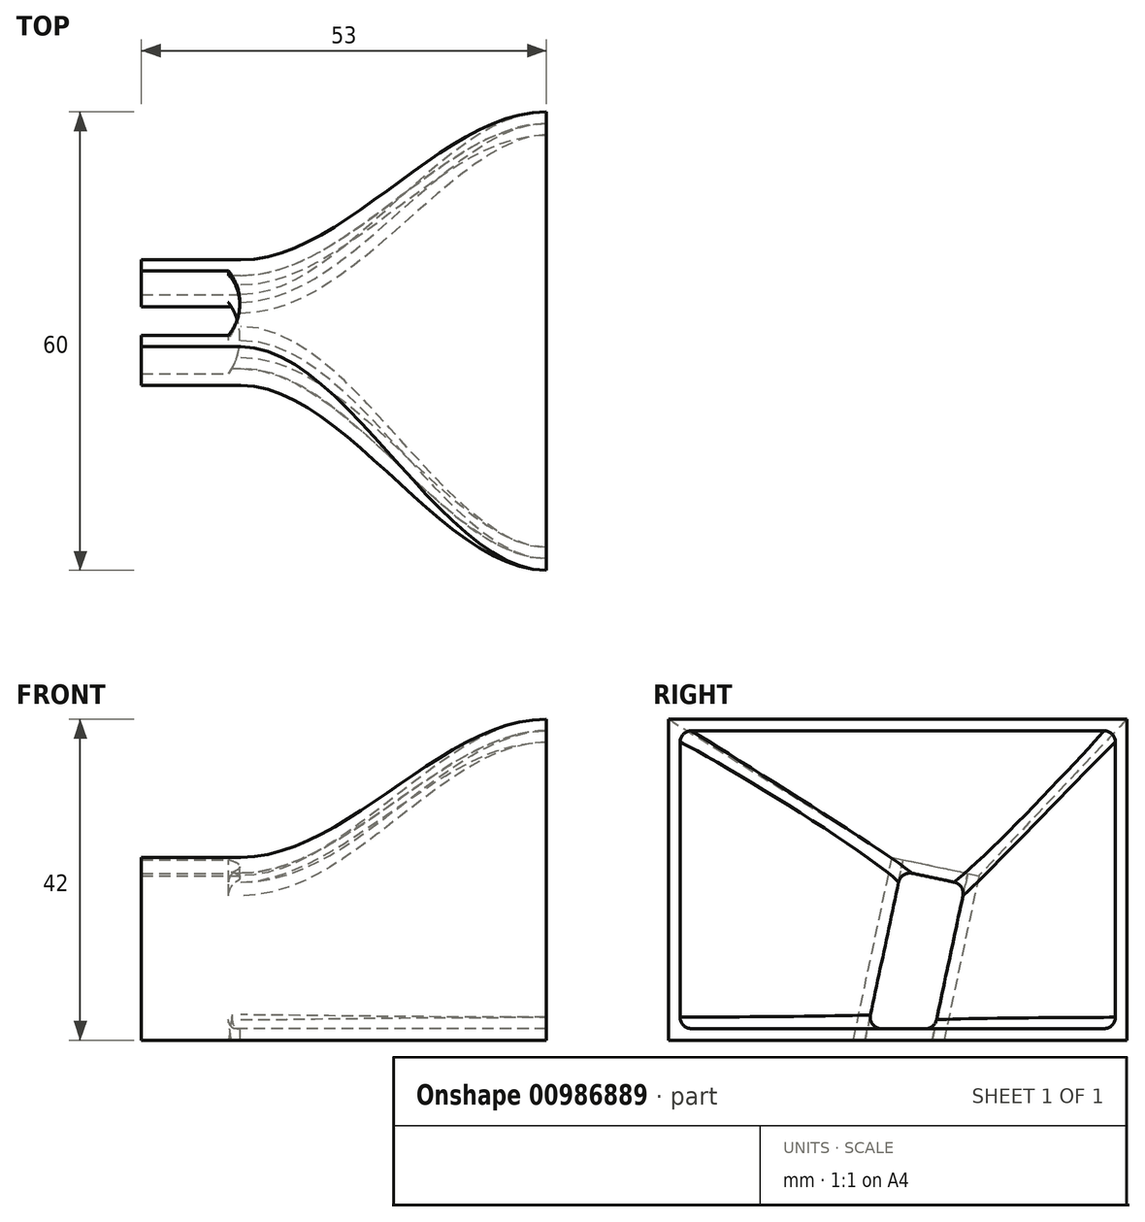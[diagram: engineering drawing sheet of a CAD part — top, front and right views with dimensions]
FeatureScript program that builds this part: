
annotation { "Feature Type Name" : "Feature", "Feature Type Description" : "" }
export const myFeature = defineFeature(function(context is Context, id is Id, definition is map)
    precondition{}
    {
        {
            var Q0;
            Q0=qCreatedBy(makeId("Top.planeOp"),FACE);
            var sketch = newSketch(context, id + "F0", { "sketchPlane" : qUnion([Q0])});
            skLineSegment(sketch, "E0", {"start": v(0, 6.05) * mm, "end": v(0, -6.05) * mm});
            skLineSegment(sketch, "E1", {"start": v(40, 30) * mm, "end": v(40, -30) * mm});
            skLineSegment(sketch, "E2", {"start": v(40, -30) * mm, "end": v(16.05, 0) * mm, "construction": true});
            skLineSegment(sketch, "E3", {"start": v(0, -6.05) * mm, "end": v(34.07, -6.05) * mm, "construction": true});
            skFitSpline(sketch, "E4", {"points": [v(0, -6.05) * mm, v(40, -30) * mm], "startDerivative": vector(33.29, 0) * mm, "endDerivative": vector(29.85, -37.4) * mm});
            skFitSpline(sketch, "E5.MirrorCS", {"points": [v(0, 6.05) * mm, v(40, 30) * mm], "startDerivative": vector(33.29, 0) * mm, "endDerivative": vector(29.85, 37.4) * mm});
            skSolve(sketch);
        }
        {
            var Q0;
            Q0=qCreatedBy(makeId("Right.planeOp"),FACE);
            var Q1;
            Q1=sQuery(id+"F0.wireOp",VERTEX,"E1.end");
            cPlane(context, id + "F1", {"entities" : qUnion([Q0, Q1]), "cplaneType" : CPlaneType.PLANE_POINT, "offset" : 25 * mm, "width" : 150 * mm, "height" : 150 * mm});
        }
        {
            var Q0;
            Q0=qCreatedBy(id+"F1.planeOp",FACE);
            var sketch = newSketch(context, id + "F2", { "sketchPlane" : qUnion([Q0])});
            skLineSegment(sketch, "E6.0", {"start": v(30, 0) * mm, "end": v(-30, 0) * mm});
            skLineSegment(sketch, "E7", {"start": v(-30, 0) * mm, "end": v(-30, 42) * mm});
            skLineSegment(sketch, "E8", {"start": v(-30, 42) * mm, "end": v(30, 42) * mm});
            skLineSegment(sketch, "E9", {"start": v(30, 42) * mm, "end": v(30, 0) * mm});
            skSolve(sketch);
        }
        {
            var Q0;
            Q0=qCreatedBy(makeId("Right.planeOp"),FACE);
            var sketch = newSketch(context, id + "F3", { "sketchPlane" : qUnion([Q0])});
            skPoint(sketch, "E10.0", {"position": v(6.05, 0) * mm});
            skLineSegment(sketch, "E11", {"start": v(-5.8, 0) * mm, "end": v(-0.72, 23.93) * mm});
            skLineSegment(sketch, "E12", {"start": v(-0.72, 23.93) * mm, "end": v(10.62, 21.52) * mm});
            skLineSegment(sketch, "E13", {"start": v(10.62, 21.52) * mm, "end": v(6.05, 0) * mm});
            skLineSegment(sketch, "E14", {"start": v(16.92, 0) * mm, "end": v(-15.5, 0) * mm, "construction": true});
            skLineSegment(sketch, "E15", {"start": v(6.05, 0) * mm, "end": v(-5.8, 0) * mm});
            skSolve(sketch);
        }
        {
            var Q0;
            Q0=sQuery(id+"F0.wireOp",EDGE,"E5.MirrorCS");
            var Q1;
            Q1=makeQuery(id+"F2.imprint","IMPRINT",FACE,{"disambiguationData":[TD([[makeQuery(id+"F2.imprint","IMPRINT",EDGE,{"derivedFrom":sQuery(id+"F2.wireOp",EDGE,"E6.0")}),-1.0]])]});
            var Q2;
            Q2=makeQuery(id+"F3.imprint","IMPRINT",FACE,{"disambiguationData":[TD([[makeQuery(id+"F3.imprint","IMPRINT",EDGE,{"derivedFrom":sQuery(id+"F3.wireOp",EDGE,"E11")}),-1.0]])]});
            var Q3;
            Q3=sQuery(id+"F0.wireOp",EDGE,"E5.MirrorCS");
            loft(context, id + "F4", {"spine" : qUnion([Q0]), "startCondition" : LoftEndDerivativeType.NORMAL_TO_PROFILE, "startMagnitude" : 1, "endCondition" : LoftEndDerivativeType.NORMAL_TO_PROFILE, "endMagnitude" : 1, "sheetProfilesArray" : [{ "sheetProfileEntities" : qUnion([Q1]) }, { "sheetProfileEntities" : qUnion([Q2]) }], "guidesArray" : [{ "guideEntities" : qUnion([Q3]), "guideDerivativeType" : LoftGuideDerivativeType.DEFAULT, "guideDerivativeMagnitude" : 1 }]});
        }
        {
            var Q0;
            Q0=makeQuery(id+"F4.opLoft","CAP_FACE",FACE,{"disambiguationData":[OSD([makeQuery(id+"F2.imprint","IMPRINT",FACE,{"disambiguationData":[TD([[makeQuery(id+"F2.imprint","IMPRINT",EDGE,{"derivedFrom":sQuery(id+"F2.wireOp",EDGE,"E6.0")}),-1.0]])]})])],"isStart":true});
            var Q1;
            Q1=makeQuery(id+"F4.opLoft","CAP_FACE",FACE,{"disambiguationData":[OSD([makeQuery(id+"F3.imprint","IMPRINT",FACE,{"disambiguationData":[TD([[makeQuery(id+"F3.imprint","IMPRINT",EDGE,{"derivedFrom":sQuery(id+"F3.wireOp",EDGE,"E11")}),-1.0]])]})])],"isStart":true});
            shell(context, id + "F5", {"entities" : qUnion([Q0, Q1]), "thickness" : 1.5 * mm});
        }
        {
            var Q0;
            Q0=qCreatedBy(makeId("Right.planeOp"),FACE);
            var sketch = newSketch(context, id + "F6", { "sketchPlane" : qUnion([Q0])});
            skLineSegment(sketch, "E16.0", {"start": v(10.62, 21.52) * mm, "end": v(6.05, 0) * mm});
            skLineSegment(sketch, "E16.3", {"start": v(-0.72, 23.93) * mm, "end": v(0.74, 23.62) * mm});
            skLineSegment(sketch, "E16.4", {"start": v(-5.8, 0) * mm, "end": v(-0.72, 23.93) * mm});
            skLineSegment(sketch, "E16.7", {"start": v(6.05, 0) * mm, "end": v(4.52, 0) * mm});
            skLineSegment(sketch, "E17.0", {"start": v(9.16, 21.83) * mm, "end": v(4.52, 0) * mm});
            skLineSegment(sketch, "E18.0", {"start": v(-4.28, 0) * mm, "end": v(0.74, 23.62) * mm});
            skLineSegment(sketch, "E19.trimOffspring", {"start": v(-4.28, 0) * mm, "end": v(-5.8, 0) * mm});
            skLineSegment(sketch, "E20.trimOffspring", {"start": v(9.16, 21.83) * mm, "end": v(10.62, 21.52) * mm});
            skSolve(sketch);
        }
        {
            var Q0;
            Q0 = qSketchRegion(id + "F6", true);
            extrude(context, id + "F7", {"entities" : qUnion([Q0]), "operationType" : NewBodyOperationType.ADD, "oppositeDirection" : true, "depth" : 13 * mm, "offsetDistance" : 25 * mm});
        }
        {
            var Q0;
            Q0=qCreatedBy(makeId("Top.planeOp"),FACE);
            var sketch = newSketch(context, id + "F8", { "sketchPlane" : qUnion([Q0])});
            skLineSegment(sketch, "E21.0", {"start": v(0, 6.05) * mm, "end": v(0, -6.05) * mm, "construction": true});
            skLineSegment(sketch, "E21.1", {"start": v(-13, 4.52) * mm, "end": v(0, 4.52) * mm, "construction": true});
            skLineSegment(sketch, "E21.2", {"start": v(-13, -4.28) * mm, "end": v(0, -4.28) * mm, "construction": true});
            skLineSegment(sketch, "E22", {"start": v(-1.5, 4.52) * mm, "end": v(0, 4.52) * mm});
            skLineSegment(sketch, "E23", {"start": v(0, 4.52) * mm, "end": v(0, -4.28) * mm});
            skLineSegment(sketch, "E24", {"start": v(-1.5, -4.28) * mm, "end": v(0, -4.28) * mm});
            skLineSegment(sketch, "E25.0", {"start": v(-13, 5.02) * mm, "end": v(0.01, 5.02) * mm, "construction": true});
            skArc(sketch, "E26", {"start": v(-1.6, -4.28) * mm, "mid": v(-0.1, 0.37) * mm, "end": v(-1.59, 5.02) * mm});
            skLineSegment(sketch, "E27", {"start": v(-1.59, 5.02) * mm, "end": v(0.01, 5.02) * mm});
            skLineSegment(sketch, "E28", {"start": v(0.01, 5.02) * mm, "end": v(0, -4.28) * mm});
            skLineSegment(sketch, "E29", {"start": v(0, -4.28) * mm, "end": v(-1.6, -4.28) * mm});
            skSolve(sketch);
        }
        {
            var Q0;
            {var subQ4=sQuery(id+"F8.wireOp",EDGE,"E23");Q0=makeQuery(id+"F8.imprint","IMPRINT",FACE,{"disambiguationData":[TD([[makeQuery(id+"F8.imprint","IMPRINT",EDGE,{"derivedFrom":subQ4}),1.0]])]});}
            var Q1;
            {var subQ0=sQuery(id+"F8.wireOp",EDGE,"E23");Q1=makeQuery(id+"F8.imprint","IMPRINT",FACE,{"disambiguationData":[TD([[makeQuery(id+"F8.imprint","IMPRINT",EDGE,{"derivedFrom":subQ0}),-1.0]])]});}
            extrude(context, id + "F9", {"entities" : qUnion([Q0, Q1]), "operationType" : NewBodyOperationType.ADD, "depth" : 1.5 * mm, "offsetDistance" : 25 * mm});
        }
        {
            var Q0;
            Q0=makeQuery(id+"F7.opExtrude","SWEPT_FACE",FACE,{"disambiguationData":[OSD([sQuery(id+"F6.wireOp",EDGE,"E16.3")])]});
            var sketch = newSketch(context, id + "F10", { "sketchPlane" : qUnion([Q0])});
            skLineSegment(sketch, "E30.0", {"start": v(-13, -4.18) * mm, "end": v(0, -4.18) * mm, "construction": true});
            skLineSegment(sketch, "E30.1", {"start": v(-13, 4.42) * mm, "end": v(0, 4.42) * mm, "construction": true});
            skLineSegment(sketch, "E30.2", {"start": v(0.01, 4.9) * mm, "end": v(0, -4.18) * mm, "construction": true});
            skArc(sketch, "E31", {"start": v(-1.6, -4.18) * mm, "mid": v(-0.12, 0.12) * mm, "end": v(-1.6, 4.42) * mm});
            skLineSegment(sketch, "E32", {"start": v(-1.6, -4.18) * mm, "end": v(0, -4.18) * mm});
            skLineSegment(sketch, "E33", {"start": v(0, -4.18) * mm, "end": v(0, 4.42) * mm});
            skLineSegment(sketch, "E34", {"start": v(0, 4.42) * mm, "end": v(-1.6, 4.42) * mm});
            skSolve(sketch);
        }
        {
            var Q0;
            Q0=makeQuery(id+"F10.imprint","IMPRINT",FACE,{"disambiguationData":[TD([[makeQuery(id+"F10.imprint","IMPRINT",EDGE,{"derivedFrom":sQuery(id+"F10.wireOp",EDGE,"E31")}),-1.0]])]});
            extrude(context, id + "F11", {"entities" : qUnion([Q0]), "operationType" : NewBodyOperationType.ADD, "oppositeDirection" : true, "depth" : 1.5 * mm, "offsetDistance" : 25 * mm});
        }
        {
            var Q0;
            Q0=makeQuery(id+"F5.opShell","OFFSET_EDGE",EDGE,{"disambiguationData":[OSD([sQuery(id+"F2.wireOp",EDGE,"E8"),sQuery(id+"F2.wireOp",EDGE,"E9"),sQuery(id+"F3.wireOp",EDGE,"E12"),sQuery(id+"F3.wireOp",EDGE,"E13")])]});
            var Q1;
            Q1=makeQuery(id+"F11.opExtrude","CAP_EDGE",EDGE,{"disambiguationData":[OSD([sQuery(id+"F10.wireOp",EDGE,"E34")])],"isStart":false});
            var Q2;
            Q2=makeQuery(id+"F5.opShell","OFFSET_EDGE",EDGE,{"disambiguationData":[OSD([sQuery(id+"F2.wireOp",EDGE,"E7"),sQuery(id+"F2.wireOp",EDGE,"E8"),sQuery(id+"F3.wireOp",EDGE,"E11"),sQuery(id+"F3.wireOp",EDGE,"E12")])]});
            var Q3;
            Q3=makeQuery(id+"F5.opShell","OFFSET_EDGE",EDGE,{"disambiguationData":[OSD([sQuery(id+"F2.wireOp",EDGE,"E6.0"),sQuery(id+"F2.wireOp",EDGE,"E7"),sQuery(id+"F3.wireOp",EDGE,"E11"),sQuery(id+"F3.wireOp",EDGE,"E15")])]});
            var Q4;
            Q4=makeQuery(id+"F5.opShell","OFFSET_EDGE",EDGE,{"disambiguationData":[OSD([sQuery(id+"F2.wireOp",EDGE,"E6.0"),sQuery(id+"F2.wireOp",EDGE,"E9"),sQuery(id+"F3.wireOp",EDGE,"E13"),sQuery(id+"F3.wireOp",EDGE,"E15")])]});
            fillet(context, id + "F12", {"entities" : qUnion([Q0, Q1, Q2, Q3, Q4]), "radius" : 1.5 * mm, "tangentPropagation" : true, "allowEdgeOverflow" : false});
        }
    });
